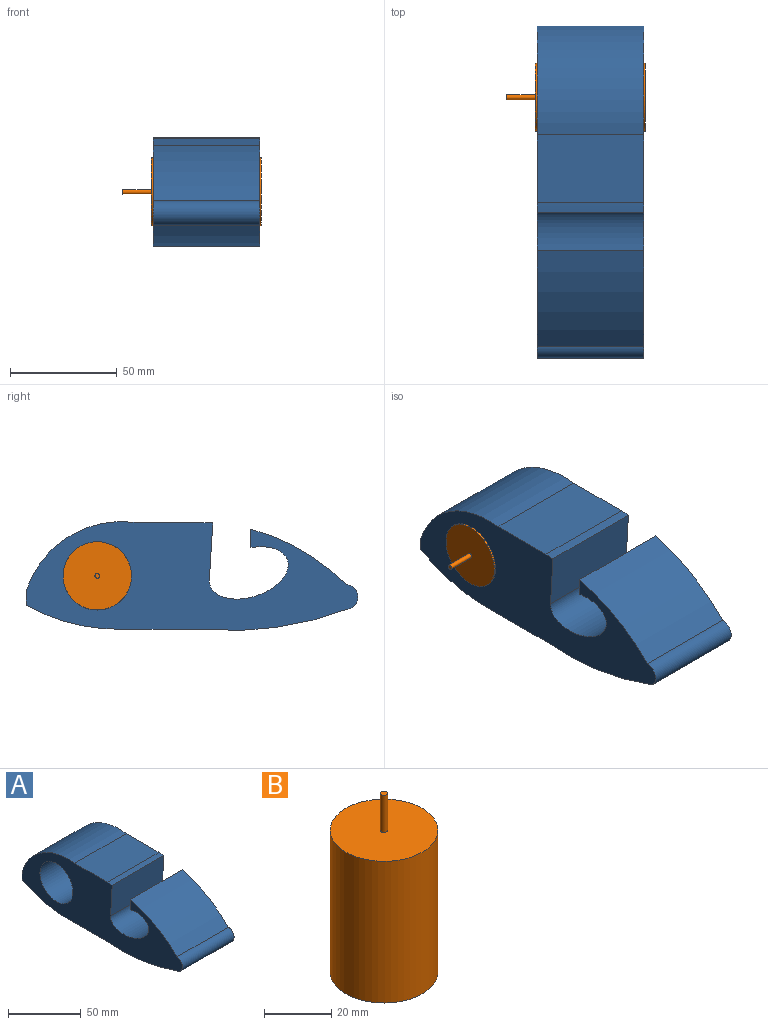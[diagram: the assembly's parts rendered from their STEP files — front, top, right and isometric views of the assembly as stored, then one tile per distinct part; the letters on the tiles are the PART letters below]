
ASSEMBLY  parts=2 mates=1
PART A: 15 faces, bbox 50x155.5x51 mm
  f0: cylinder r=149.27mm len=66.43mm, axis (-1,0,0), area 3382.7mm2, adj f1,f11,f13,f14
  f1: plane 50x38.77mm, normal (0,0,-1), area 1938.5mm2, adj f0,f2,f13,f14
  f2: cylinder r=89.01mm len=50mm, axis (-1,0,0), area 2336.8mm2, adj f1,f3,f13,f14
  f3: plane 50x6.36mm, normal (0,1,0), area 318.1mm2, adj f2,f4,f13,f14
  f4: cylinder r=47.01mm len=51.06mm, axis (-1,0,0), area 3283mm2, adj f3,f5,f13,f14
  f5: plane 50x31.74mm, normal (0,0,1), area 1587mm2, adj f4,f6,f13,f14
  f6: cylinder r=97.63mm len=50mm, axis (-1,0,0), area 231.4mm2, adj f5,f7,f13,f14
  f7: plane 50x26.62mm, normal (0,-1,-0.06), area 1333.3mm2, adj f6,f8,f13,f14
  f8: extruded ~50x36.9mm, area 3542.2mm2, adj f7,f9,f13,f14
  f9: plane 50x8.52mm, normal (0,1,0), area 426.1mm2, adj f8,f10,f13,f14
  f10: cylinder r=97.63mm len=50mm, axis (-1,0,0), area 2615.5mm2, adj f9,f11,f13,f14
  f11: cylinder r=5.77mm len=50mm, axis (-1,0,0), area 874.5mm2, adj f0,f10,f13,f14
  f12: cylinder r=16mm len=50mm, axis (-1,0,0), area 5026.5mm2, adj f13,f14
  f13: plane 155.45x50.99mm, normal (1,0,0), area 4503.8mm2, adj f0,f1,f2,f3,f4,f5,f6,f7
  f14: plane 155.45x50.99mm, normal (-1,0,0), area 4503.8mm2, adj f0,f1,f2,f3,f4,f5,f6,f7
PART B: 5 faces, bbox 32x32x65 mm
  f0: plane 2.2x2.2mm, normal (0,0,1), area 3.8mm2, adj f4
  f1: plane 32x32mm, normal (0,0,-1), area 804.2mm2, adj f2
  f2: cylinder r=16mm len=51.5mm, axis (0,0,1), area 5177.3mm2, adj f1,f3
  f3: plane 32x32mm, normal (0,0,1), area 800.4mm2, adj f2,f4
  f4: cylinder r=1.1mm len=13.5mm, axis (0,0,1), area 93.3mm2, adj f0,f3
PLACE A t=(-14.36,15.65,-11.07)mm
PLACE B rot(axis=(0,-1,0),90deg) t=(11.99,147.88,13.93)mm
MATE fastened B.f2 <-> A.f12  axis (-1,0,0) through (10.64,132.26,13.93)mm
